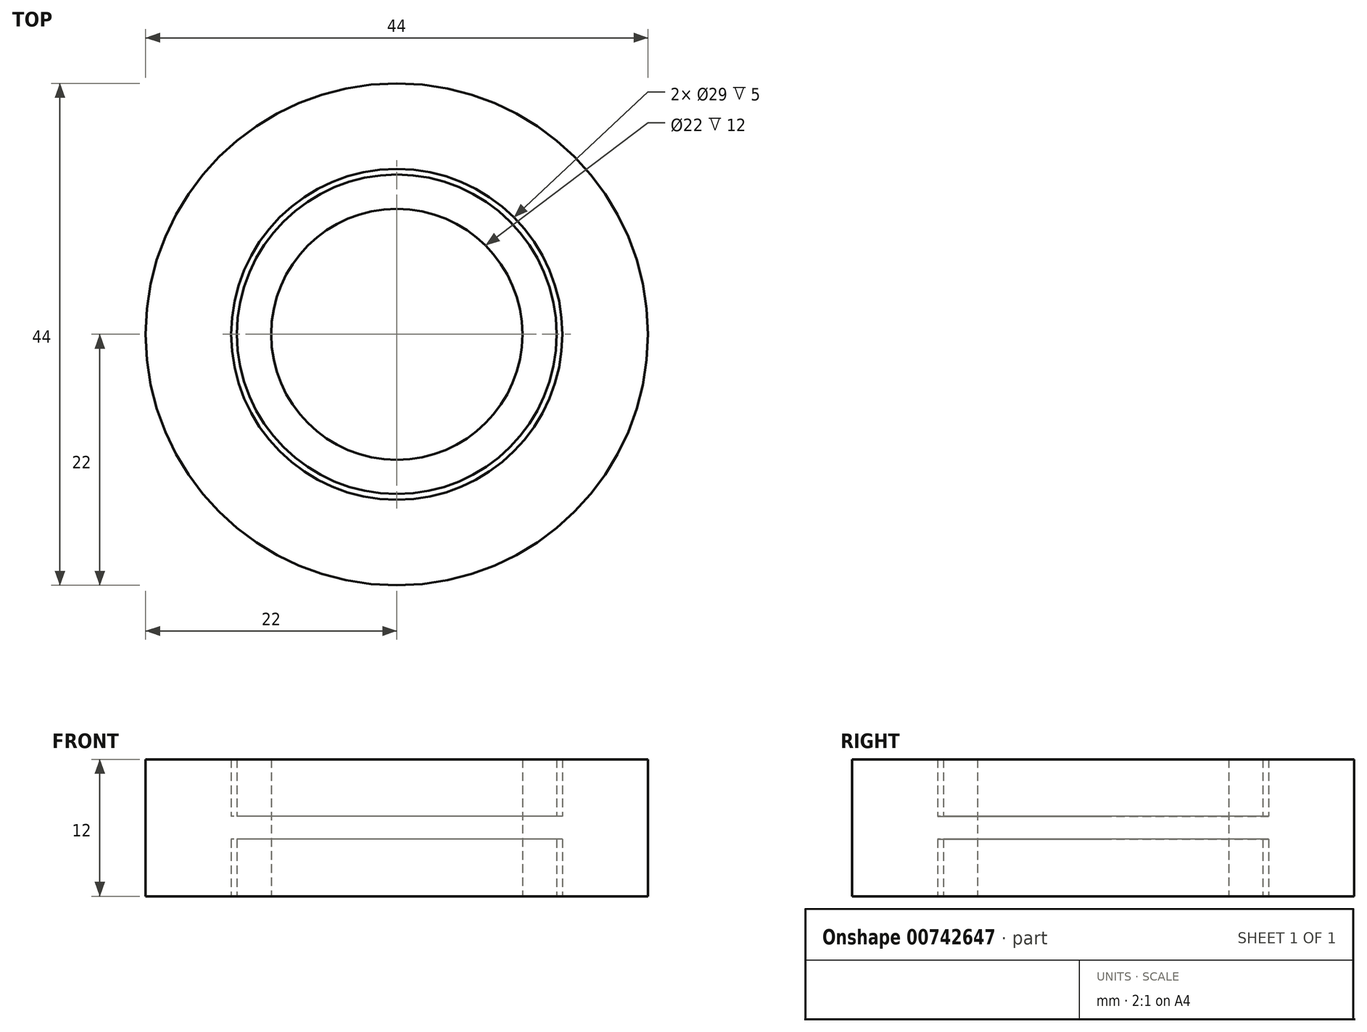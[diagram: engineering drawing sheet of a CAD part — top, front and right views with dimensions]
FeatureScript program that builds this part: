
annotation { "Feature Type Name" : "Feature", "Feature Type Description" : "" }
export const myFeature = defineFeature(function(context is Context, id is Id, definition is map)
    precondition{}
    {
        {
            assignVariable(context, id + "F0", {"name" : "BearingHeight", "anyValue" : 12});
        }
        {
            var Q0;
            Q0=qCreatedBy(makeId("Top.planeOp"),FACE);
            var sketch = newSketch(context, id + "F1", { "sketchPlane" : qUnion([Q0])});
            skCircle(sketch, "E0", {"center": v(0, 0) * mm, "radius": 11 * mm});
            skCircle(sketch, "E1", {"center": v(0, 0) * mm, "radius": 22 * mm});
            skCircle(sketch, "E2", {"center": v(0, 0) * mm, "radius": 14 * mm});
            skCircle(sketch, "E3", {"center": v(0, 0) * mm, "radius": 14.5 * mm});
            skSolve(sketch);
        }
        {
            var Q0;
            Q0=makeQuery(id+"F1.imprint","IMPRINT",FACE,{"disambiguationData":[TD([[makeQuery(id+"F1.imprint","IMPRINT",EDGE,{"derivedFrom":sQuery(id+"F1.wireOp",EDGE,"E0")}),-1.0]])]});
            var Q1;
            Q1=makeQuery(id+"F1.imprint","IMPRINT",FACE,{"disambiguationData":[TD([[makeQuery(id+"F1.imprint","IMPRINT",EDGE,{"derivedFrom":sQuery(id+"F1.wireOp",EDGE,"E1")}),1.0]])]});
            extrude(context, id + "F2", {"entities" : qUnion([Q0, Q1]), "depth" : (getVariable(context, 'BearingHeight')) * mm, "offsetDistance" : 25 * mm});
        }
        {
            var Q0;
            Q0=makeQuery(id+"F2.opExtrude","CAP_FACE",FACE,{"disambiguationData":[OSD([sQuery(id+"F1.wireOp",EDGE,"E1"),sQuery(id+"F1.wireOp",EDGE,"E3")])],"isStart":false});
            var Q1;
            Q1=makeQuery(id+"F2.opExtrude","CAP_FACE",FACE,{"disambiguationData":[OSD([sQuery(id+"F1.wireOp",EDGE,"E1"),sQuery(id+"F1.wireOp",EDGE,"E3")])],"isStart":true});
            cPlane(context, id + "F3", {"entities" : qUnion([Q0, Q1]), "cplaneType" : CPlaneType.MID_PLANE, "offset" : 25 * mm, "width" : 150 * mm, "height" : 150 * mm});
        }
        {
            var Q0;
            Q0=qCreatedBy(id+"F3.planeOp",FACE);
            var sketch = newSketch(context, id + "F4", { "sketchPlane" : qUnion([Q0])});
            skCircle(sketch, "E4", {"center": v(0, 0) * mm, "radius": 12.5 * mm});
            skCircle(sketch, "E5", {"center": v(0, 0) * mm, "radius": 18.25 * mm});
            skLineSegment(sketch, "E6", {"start": v(-14, 0) * mm, "end": v(-11, 0) * mm, "construction": true});
            skLineSegment(sketch, "E7", {"start": v(-22, 0) * mm, "end": v(-14.5, 0) * mm, "construction": true});
            skPoint(sketch, "E8", {"position": v(-18.25, 0) * mm});
            skPoint(sketch, "E9", {"position": v(-12.5, 0) * mm});
            skSolve(sketch);
        }
        {
            var Q0;
            Q0=makeQuery(id+"F4.imprint","IMPRINT",FACE,{"disambiguationData":[TD([[makeQuery(id+"F4.imprint","IMPRINT",EDGE,{"derivedFrom":sQuery(id+"F4.wireOp",EDGE,"E4")}),-1.0]])]});
            extrude(context, id + "F5", {"entities" : qUnion([Q0]), "operationType" : NewBodyOperationType.ADD, "depth" : 1 * mm, "offsetDistance" : 25 * mm, "hasSecondDirection" : true, "secondDirectionOppositeDirection" : true, "secondDirectionDepth" : 1 * mm});
        }
    });
